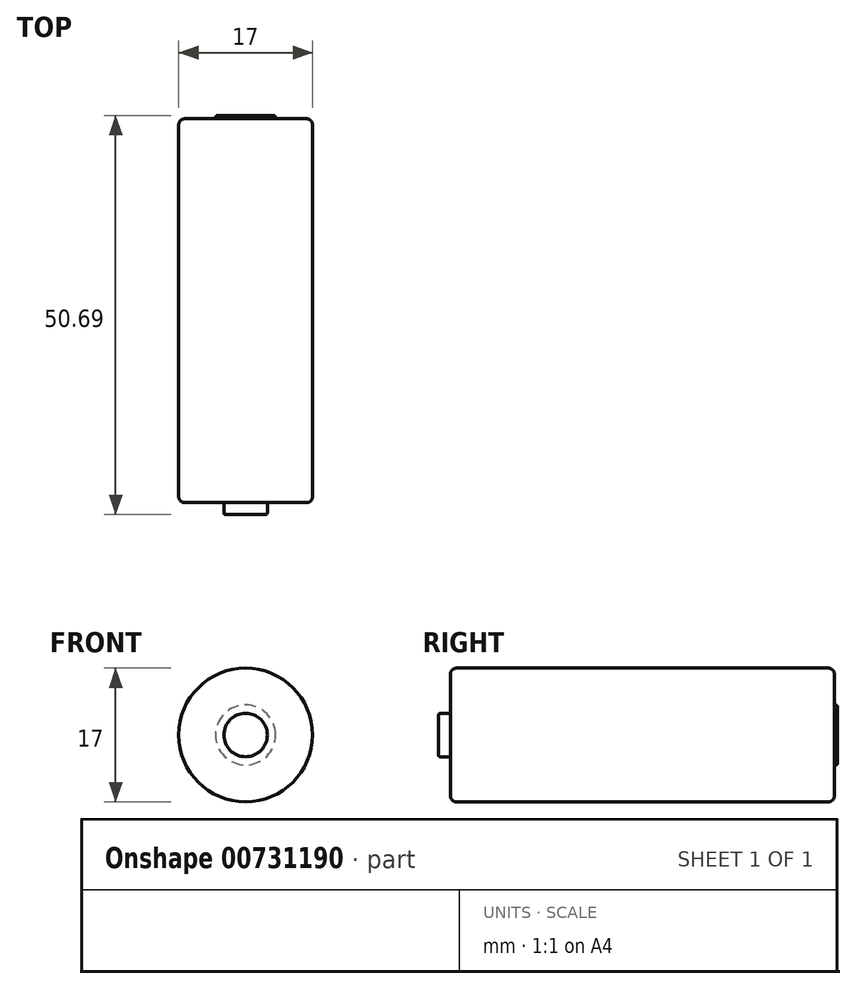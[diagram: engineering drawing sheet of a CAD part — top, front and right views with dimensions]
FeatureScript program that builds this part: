
annotation { "Feature Type Name" : "Feature", "Feature Type Description" : "" }
export const myFeature = defineFeature(function(context is Context, id is Id, definition is map)
    precondition{}
    {
        {
            var Q0;
            Q0=qCreatedBy(makeId("Front.planeOp"),FACE);
            var sketch = newSketch(context, id + "F0", { "sketchPlane" : qUnion([Q0])});
            skCircle(sketch, "E0", {"center": v(0, 0) * mm, "radius": 8.5 * mm});
            skSolve(sketch);
        }
        {
            var Q0;
            Q0=makeQuery(id+"F0.imprint","IMPRINT",FACE,{"disambiguationData":[TD([[makeQuery(id+"F0.imprint","IMPRINT",EDGE,{"derivedFrom":sQuery(id+"F0.wireOp",EDGE,"E0")}),1.0]])]});
            extrude(context, id + "F1", {"entities" : qUnion([Q0]), "oppositeDirection" : true, "depth" : 48.77 * mm, "offsetDistance" : 25.4 * mm});
        }
        {
            var Q0;
            Q0=makeQuery(id+"F0.imprint","IMPRINT",FACE,{"disambiguationData":[TD([[makeQuery(id+"F0.imprint","IMPRINT",EDGE,{"derivedFrom":sQuery(id+"F0.wireOp",EDGE,"E0")}),1.0]])]});
            var sketch = newSketch(context, id + "F2", { "sketchPlane" : qUnion([Q0])});
            skCircle(sketch, "E1", {"center": v(0, 0) * mm, "radius": 2.76 * mm});
            skSolve(sketch);
        }
        {
            var Q0;
            Q0 = qSketchRegion(id + "F2", true);
            extrude(context, id + "F3", {"entities" : qUnion([Q0]), "operationType" : NewBodyOperationType.ADD, "depth" : 1.52 * mm, "offsetDistance" : 25.4 * mm});
        }
        {
            var Q0;
            Q0=makeQuery(id+"F1.opExtrude","CAP_FACE",FACE,{"disambiguationData":[OSD([sQuery(id+"F0.wireOp",EDGE,"E0")])],"isStart":false});
            var sketch = newSketch(context, id + "F4", { "sketchPlane" : qUnion([Q0])});
            skCircle(sketch, "E2", {"center": v(0, 0) * mm, "radius": 3.8 * mm});
            skSolve(sketch);
        }
        {
            var Q0;
            Q0 = qSketchRegion(id + "F4", true);
            extrude(context, id + "F5", {"entities" : qUnion([Q0]), "operationType" : NewBodyOperationType.ADD, "depth" : 0.4 * mm, "offsetDistance" : 25.4 * mm});
        }
        {
            var Q0;
            Q0=makeQuery(id+"F5.opExtrude","CAP_EDGE",EDGE,{"disambiguationData":[OSD([sQuery(id+"F4.wireOp",EDGE,"E2")])],"isStart":false});
            var Q1;
            Q1=makeQuery(id+"F3.opExtrude","CAP_EDGE",EDGE,{"disambiguationData":[OSD([sQuery(id+"F2.wireOp",EDGE,"E1")])],"isStart":false});
            fillet(context, id + "F6", {"entities" : qUnion([Q0, Q1]), "tangentPropagation" : true, "radius" : 0.25 * mm, "defaultsChanged" : true, "vertexSettings" : [], "allowEdgeOverflow" : false});
        }
        {
            var Q0;
            Q0=makeQuery(id+"F1.opExtrude","CAP_EDGE",EDGE,{"disambiguationData":[OSD([sQuery(id+"F0.wireOp",EDGE,"E0")])],"isStart":false});
            var Q1;
            Q1=makeQuery(id+"F1.opExtrude","CAP_EDGE",EDGE,{"disambiguationData":[OSD([sQuery(id+"F0.wireOp",EDGE,"E0")])],"isStart":true});
            fillet(context, id + "F7", {"entities" : qUnion([Q0, Q1]), "tangentPropagation" : true, "radius" : 0.76 * mm, "defaultsChanged" : true, "vertexSettings" : [], "allowEdgeOverflow" : false});
        }
    });
